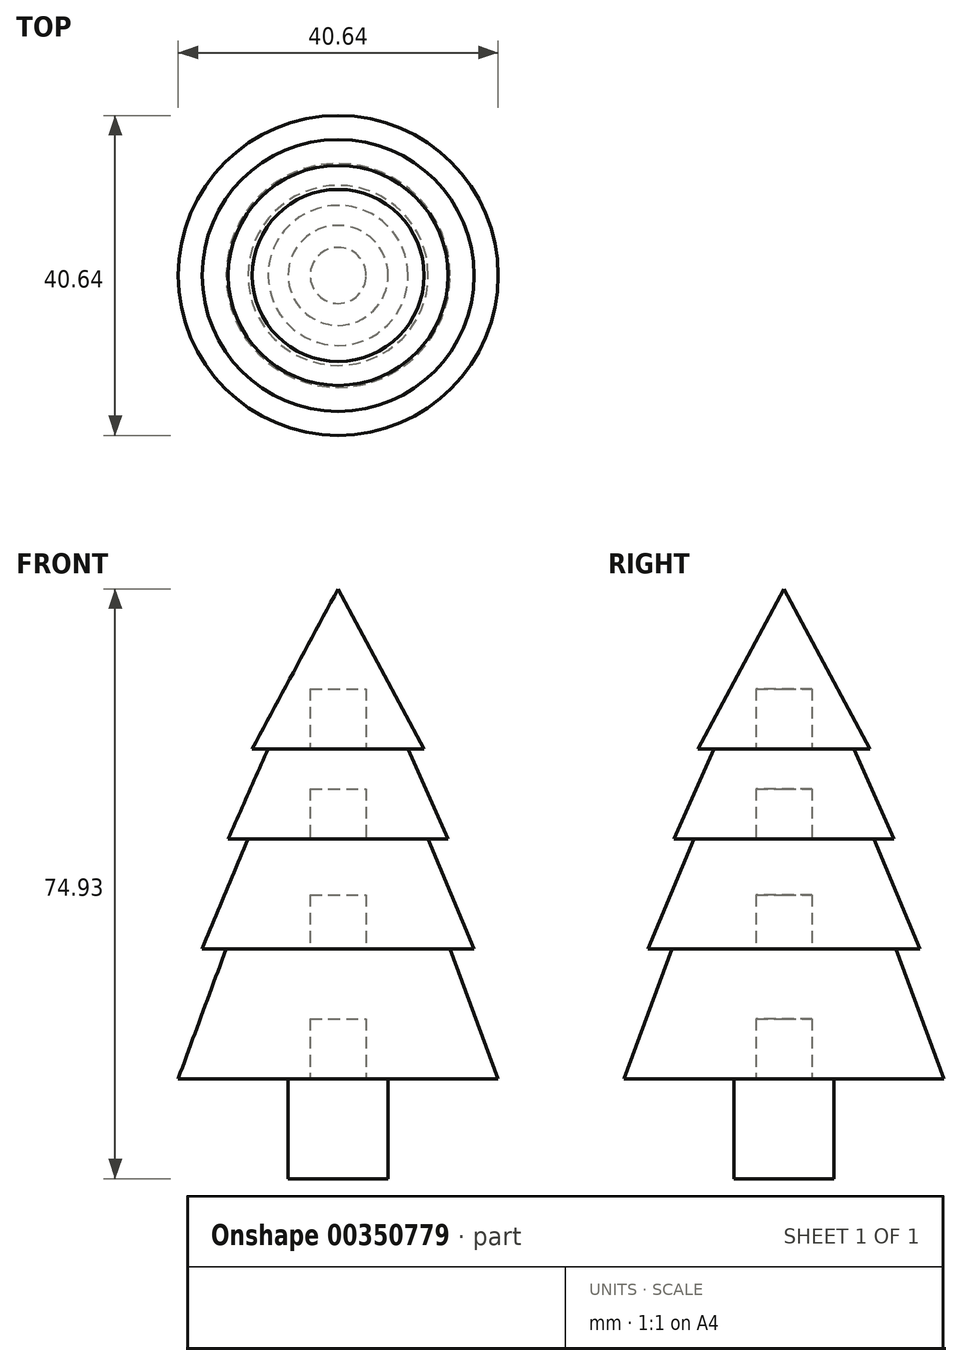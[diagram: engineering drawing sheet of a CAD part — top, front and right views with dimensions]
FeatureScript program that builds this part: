
annotation { "Feature Type Name" : "Feature", "Feature Type Description" : "" }
export const myFeature = defineFeature(function(context is Context, id is Id, definition is map)
    precondition{}
    {
        {
            var Q0;
            Q0=qCreatedBy(makeId("Top.planeOp"),FACE);
            var sketch = newSketch(context, id + "F0", { "sketchPlane" : qUnion([Q0])});
            skCircle(sketch, "E0", {"center": v(0, 0) * mm, "radius": 6.35 * mm});
            skSolve(sketch);
        }
        {
            var Q0;
            Q0=makeQuery(id+"F0.imprint","IMPRINT",FACE,{"disambiguationData":[TD([[makeQuery(id+"F0.imprint","IMPRINT",EDGE,{"derivedFrom":sQuery(id+"F0.wireOp",EDGE,"E0")}),1.0]])]});
            extrude(context, id + "F1", {"entities" : qUnion([Q0]), "depth" : 12.7 * mm});
        }
        {
            var Q0;
            Q0=makeQuery(id+"F1.opExtrude","CAP_FACE",FACE,{"disambiguationData":[OSD([sQuery(id+"F0.wireOp",EDGE,"E0")])],"isStart":false});
            var sketch = newSketch(context, id + "F2", { "sketchPlane" : qUnion([Q0])});
            skCircle(sketch, "E1", {"center": v(0, 0) * mm, "radius": 3.18 * mm});
            skSolve(sketch);
        }
        {
            var Q0;
            Q0 = qSketchRegion(id + "F2", true);
            extrude(context, id + "F3", {"entities" : qUnion([Q0]), "operationType" : NewBodyOperationType.ADD, "depth" : 6.35 * mm});
        }
        {
            var Q0;
            Q0=qCreatedBy(makeId("Front.planeOp"),FACE);
            var sketch = newSketch(context, id + "F4", { "sketchPlane" : qUnion([Q0])});
            skLineSegment(sketch, "E2", {"start": v(0, 12.7) * mm, "end": v(0, 29.21) * mm});
            skLineSegment(sketch, "E3", {"start": v(0, 29.21) * mm, "end": v(14.22, 29.21) * mm});
            skLineSegment(sketch, "E4", {"start": v(14.22, 29.21) * mm, "end": v(20.32, 12.7) * mm});
            skLineSegment(sketch, "E5", {"start": v(20.32, 12.7) * mm, "end": v(0, 12.7) * mm});
            skSolve(sketch);
        }
        {
            var Q0;
            Q0 = qSketchRegion(id + "F4", true);
            var Q1;
            Q1=sQuery(id+"F4.wireOp",EDGE,"E2");
            revolve(context, id + "F5", {"entities" : qUnion([Q0]), "axis" : qUnion([Q1]), "revolveType" : RevolveType.FULL});
        }
        {
            var Q0;
            Q0=makeQuery(id+"F5.opRevolve","SWEPT_FACE",FACE,{"disambiguationData":[OSD([sQuery(id+"F4.wireOp",EDGE,"E5")])]});
            var sketch = newSketch(context, id + "F6", { "sketchPlane" : qUnion([Q0])});
            skCircle(sketch, "E6", {"center": v(0, 0) * mm, "radius": 3.56 * mm});
            skSolve(sketch);
        }
        {
            var Q0;
            Q0 = qSketchRegion(id + "F6", true);
            var Q1;
            Q1=sQuery(id+"F6.wireOp",EDGE,"E6");
            extrude(context, id + "F7", {"entities" : qUnion([Q0]), "operationType" : NewBodyOperationType.REMOVE, "surfaceEntities" : qUnion([Q1]), "oppositeDirection" : true, "depth" : 7.62 * mm});
        }
        {
            var Q0;
            Q0=makeQuery(id+"F5.opRevolve","SWEPT_FACE",FACE,{"disambiguationData":[OSD([sQuery(id+"F4.wireOp",EDGE,"E3")])]});
            var sketch = newSketch(context, id + "F8", { "sketchPlane" : qUnion([Q0])});
            skCircle(sketch, "E7", {"center": v(0, 0) * mm, "radius": 3.18 * mm});
            skSolve(sketch);
        }
        {
            var Q0;
            Q0 = qSketchRegion(id + "F8", true);
            extrude(context, id + "F9", {"entities" : qUnion([Q0]), "operationType" : NewBodyOperationType.ADD, "depth" : 6.35 * mm});
        }
        {
            var Q0;
            Q0=qCreatedBy(makeId("Right.planeOp"),FACE);
            var sketch = newSketch(context, id + "F10", { "sketchPlane" : qUnion([Q0])});
            skLineSegment(sketch, "E8", {"start": v(0, 43.18) * mm, "end": v(-11.43, 43.18) * mm});
            skLineSegment(sketch, "E9", {"start": v(-11.43, 43.18) * mm, "end": v(-17.27, 29.21) * mm});
            skLineSegment(sketch, "E10", {"start": v(-17.27, 29.21) * mm, "end": v(0, 29.21) * mm});
            skLineSegment(sketch, "E11", {"start": v(0, 29.21) * mm, "end": v(0, 43.18) * mm});
            skSolve(sketch);
        }
        {
            var Q0;
            Q0=makeQuery(id+"F10.imprint","IMPRINT",FACE,{"disambiguationData":[TD([[makeQuery(id+"F10.imprint","IMPRINT",EDGE,{"derivedFrom":sQuery(id+"F10.wireOp",EDGE,"E8")}),1.0]])]});
            var Q1;
            Q1 = qConstructionFilter(qBodyType(qCreatedBy(id + "F10" ,EDGE), BodyType.WIRE), ConstructionObject.NO);
            var Q2;
            Q2=sQuery(id+"F10.wireOp",EDGE,"E11");
            revolve(context, id + "F11", {"entities" : qUnion([Q0]), "surfaceEntities" : qUnion([Q1]), "axis" : qUnion([Q2]), "revolveType" : RevolveType.FULL});
        }
        {
            var Q0;
            Q0=makeQuery(id+"F11.opRevolve","SWEPT_FACE",FACE,{"disambiguationData":[OSD([sQuery(id+"F10.wireOp",EDGE,"E10")])]});
            var sketch = newSketch(context, id + "F12", { "sketchPlane" : qUnion([Q0])});
            skCircle(sketch, "E12", {"center": v(0, 0) * mm, "radius": 3.56 * mm});
            skSolve(sketch);
        }
        {
            var Q0;
            Q0=makeQuery(id+"F12.imprint","IMPRINT",FACE,{"disambiguationData":[TD([[makeQuery(id+"F12.imprint","IMPRINT",EDGE,{"derivedFrom":sQuery(id+"F12.wireOp",EDGE,"E12")}),1.0]])]});
            var Q1;
            Q1=sQuery(id+"F12.wireOp",EDGE,"E12");
            extrude(context, id + "F13", {"entities" : qUnion([Q0]), "operationType" : NewBodyOperationType.REMOVE, "surfaceEntities" : qUnion([Q1]), "oppositeDirection" : true, "depth" : 6.86 * mm});
        }
        {
            var Q0;
            Q0=makeQuery(id+"F11.opRevolve","SWEPT_FACE",FACE,{"disambiguationData":[OSD([sQuery(id+"F10.wireOp",EDGE,"E8")])]});
            var sketch = newSketch(context, id + "F14", { "sketchPlane" : qUnion([Q0])});
            skCircle(sketch, "E13", {"center": v(0, 0) * mm, "radius": 3.18 * mm});
            skSolve(sketch);
        }
        {
            var Q0;
            Q0 = qSketchRegion(id + "F14", true);
            extrude(context, id + "F15", {"entities" : qUnion([Q0]), "operationType" : NewBodyOperationType.ADD, "depth" : 5.08 * mm});
        }
        {
            var Q0;
            Q0=qCreatedBy(makeId("Front.planeOp"),FACE);
            var sketch = newSketch(context, id + "F16", { "sketchPlane" : qUnion([Q0])});
            skLineSegment(sketch, "E14", {"start": v(0, 54.61) * mm, "end": v(8.9, 54.61) * mm});
            skLineSegment(sketch, "E15", {"start": v(8.9, 54.61) * mm, "end": v(13.97, 43.18) * mm});
            skLineSegment(sketch, "E16", {"start": v(13.97, 43.18) * mm, "end": v(0, 43.18) * mm});
            skLineSegment(sketch, "E17", {"start": v(0, 43.18) * mm, "end": v(0, 54.61) * mm});
            skSolve(sketch);
        }
        {
            var Q0;
            Q0 = qSketchRegion(id + "F16", true);
            var Q1;
            Q1=sQuery(id+"F16.wireOp",EDGE,"E17");
            revolve(context, id + "F17", {"entities" : qUnion([Q0]), "axis" : qUnion([Q1]), "revolveType" : RevolveType.FULL});
        }
        {
            var Q0;
            Q0=makeQuery(id+"F17.opRevolve","SWEPT_FACE",FACE,{"disambiguationData":[OSD([sQuery(id+"F16.wireOp",EDGE,"E16")])]});
            var sketch = newSketch(context, id + "F18", { "sketchPlane" : qUnion([Q0])});
            skCircle(sketch, "E18", {"center": v(0, 0) * mm, "radius": 3.56 * mm});
            skSolve(sketch);
        }
        {
            var Q0;
            Q0 = qSketchRegion(id + "F18", true);
            extrude(context, id + "F19", {"entities" : qUnion([Q0]), "operationType" : NewBodyOperationType.REMOVE, "oppositeDirection" : true, "depth" : 6.35 * mm});
        }
        {
            var Q0;
            Q0=makeQuery(id+"F17.opRevolve","SWEPT_FACE",FACE,{"disambiguationData":[OSD([sQuery(id+"F16.wireOp",EDGE,"E14")])]});
            var sketch = newSketch(context, id + "F20", { "sketchPlane" : qUnion([Q0])});
            skCircle(sketch, "E19", {"center": v(0, 0) * mm, "radius": 3.18 * mm});
            skSolve(sketch);
        }
        {
            var Q0;
            Q0 = qSketchRegion(id + "F20", true);
            extrude(context, id + "F21", {"entities" : qUnion([Q0]), "operationType" : NewBodyOperationType.ADD, "depth" : 3.8 * mm});
        }
        {
            var Q0;
            Q0=qCreatedBy(makeId("Front.planeOp"),FACE);
            var sketch = newSketch(context, id + "F22", { "sketchPlane" : qUnion([Q0])});
            skLineSegment(sketch, "E20", {"start": v(0, 74.93) * mm, "end": v(10.92, 54.61) * mm});
            skLineSegment(sketch, "E21", {"start": v(10.92, 54.61) * mm, "end": v(0, 54.61) * mm});
            skLineSegment(sketch, "E22", {"start": v(0, 54.61) * mm, "end": v(0, 74.93) * mm});
            skSolve(sketch);
        }
        {
            var Q0;
            Q0 = qSketchRegion(id + "F22", true);
            var Q1;
            Q1=sQuery(id+"F22.wireOp",EDGE,"E22");
            revolve(context, id + "F23", {"entities" : qUnion([Q0]), "axis" : qUnion([Q1]), "revolveType" : RevolveType.FULL});
        }
        {
            var Q0;
            Q0=makeQuery(id+"F23.opRevolve","SWEPT_FACE",FACE,{"disambiguationData":[OSD([sQuery(id+"F22.wireOp",EDGE,"E21")])]});
            var sketch = newSketch(context, id + "F24", { "sketchPlane" : qUnion([Q0])});
            skCircle(sketch, "E23", {"center": v(0, 0) * mm, "radius": 3.56 * mm});
            skSolve(sketch);
        }
        {
            var Q0;
            Q0=makeQuery(id+"F24.imprint","IMPRINT",FACE,{"disambiguationData":[TD([[makeQuery(id+"F24.imprint","IMPRINT",EDGE,{"derivedFrom":sQuery(id+"F24.wireOp",EDGE,"E23")}),1.0]])]});
            extrude(context, id + "F25", {"entities" : qUnion([Q0]), "operationType" : NewBodyOperationType.REMOVE, "oppositeDirection" : true, "depth" : 7.62 * mm});
        }
    });
